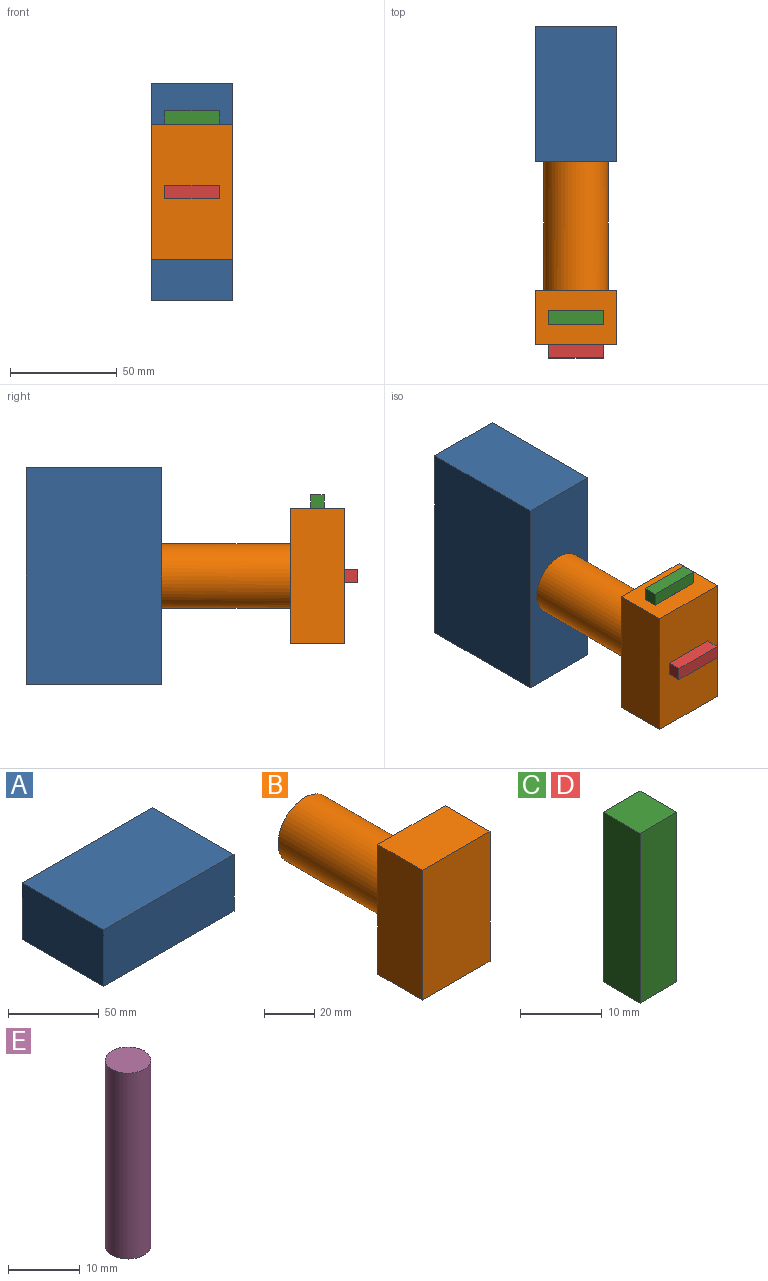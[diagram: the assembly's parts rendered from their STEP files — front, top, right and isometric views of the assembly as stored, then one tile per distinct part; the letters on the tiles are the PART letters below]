
ASSEMBLY  parts=5 mates=4
PART A: 6 faces, bbox 101.6x63.5x38.1 mm
  f0: plane 101.6x38.1mm, normal (0,1,0), area 3871mm2, adj f1,f3,f4,f5
  f1: plane 101.6x63.5mm, normal (0,0,1), area 6451.6mm2, adj f0,f2,f4,f5
  f2: plane 101.6x38.1mm, normal (0,-1,0), area 3871mm2, adj f1,f3,f4,f5
  f3: plane 101.6x63.5mm, normal (0,0,-1), area 6451.6mm2, adj f0,f2,f4,f5
  f4: plane 63.5x38.1mm, normal (1,0,0), area 2419.3mm2, adj f0,f1,f2,f3
  f5: plane 63.5x38.1mm, normal (-1,0,0), area 2419.3mm2, adj f0,f1,f2,f3
PART B: 8 faces, bbox 38.1x85.7x63.5 mm
  f0: plane 63.5x38.1mm, normal (0,1,0), area 1706.9mm2, adj f1,f3,f4,f5,f6
  f1: plane 38.1x25.33mm, normal (0,0,1), area 965mm2, adj f0,f2,f4,f5
  f2: plane 63.5x38.1mm, normal (0,-1,0), area 2419.3mm2, adj f1,f3,f4,f5
  f3: plane 38.1x25.33mm, normal (0,0,-1), area 965mm2, adj f0,f2,f4,f5
  f4: plane 63.5x25.33mm, normal (1,0,0), area 1608.3mm2, adj f0,f1,f2,f3
  f5: plane 63.5x25.33mm, normal (-1,0,0), area 1608.3mm2, adj f0,f1,f2,f3
  f6: cylinder r=15.06mm len=60.41mm, axis (0,1,0), area 5715.4mm2, adj f0,f7
  f7: plane 30.12x30.12mm, normal (0,1,0), area 712.4mm2, adj f6
PART C: 6 faces, bbox 6.4x6.4x25.4 mm
  f0: plane 25.4x6.35mm, normal (1,0,0), area 161.3mm2, adj f1,f3,f4,f5
  f1: plane 6.35x6.35mm, normal (0,0,1), area 40.3mm2, adj f0,f2,f4,f5
  f2: plane 25.4x6.35mm, normal (-1,0,0), area 161.3mm2, adj f1,f3,f4,f5
  f3: plane 6.35x6.35mm, normal (0,0,-1), area 40.3mm2, adj f0,f2,f4,f5
  f4: plane 25.4x6.35mm, normal (0,-1,0), area 161.3mm2, adj f0,f1,f2,f3
  f5: plane 25.4x6.35mm, normal (0,1,0), area 161.3mm2, adj f0,f1,f2,f3
PART D: same geometry as C
PART E: 3 faces, bbox 6.4x6.4x31.8 mm
  f0: cylinder r=3.17mm len=31.75mm, axis (0,0,-1), area 633.4mm2, adj f1,f2
  f1: plane 6.35x6.35mm, normal (0,0,1), area 31.7mm2, adj f0
  f2: plane 6.35x6.35mm, normal (0,0,-1), area 31.7mm2, adj f0
PLACE A rot(axis=(0,1,0),90deg) t=(0,31.75,0)mm
PLACE B at identity fixed
PLACE C rot(axis=(-0.58,0.58,-0.58),120deg) t=(0,-73.07,-53.98)mm
PLACE D rot(axis=(0,-1,0),90deg) t=(0,0,0)mm
PLACE E t=(0,-73.07,-19.05)mm
MATE slider C.f4 <-> B.f1  axis (0,0,1) through (0,-73.07,38.1)mm
MATE revolute B.f6 <-> D.f5  axis (0,-1,0) through (0,-85.73,0)mm
MATE revolute A.f2 <-> B.f6  axis (0,-1,0) through (0,0,0)mm
MATE fastened C.f5 <-> E.f0  axis (0,0,-1) through (0,-73.07,31.75)mm
